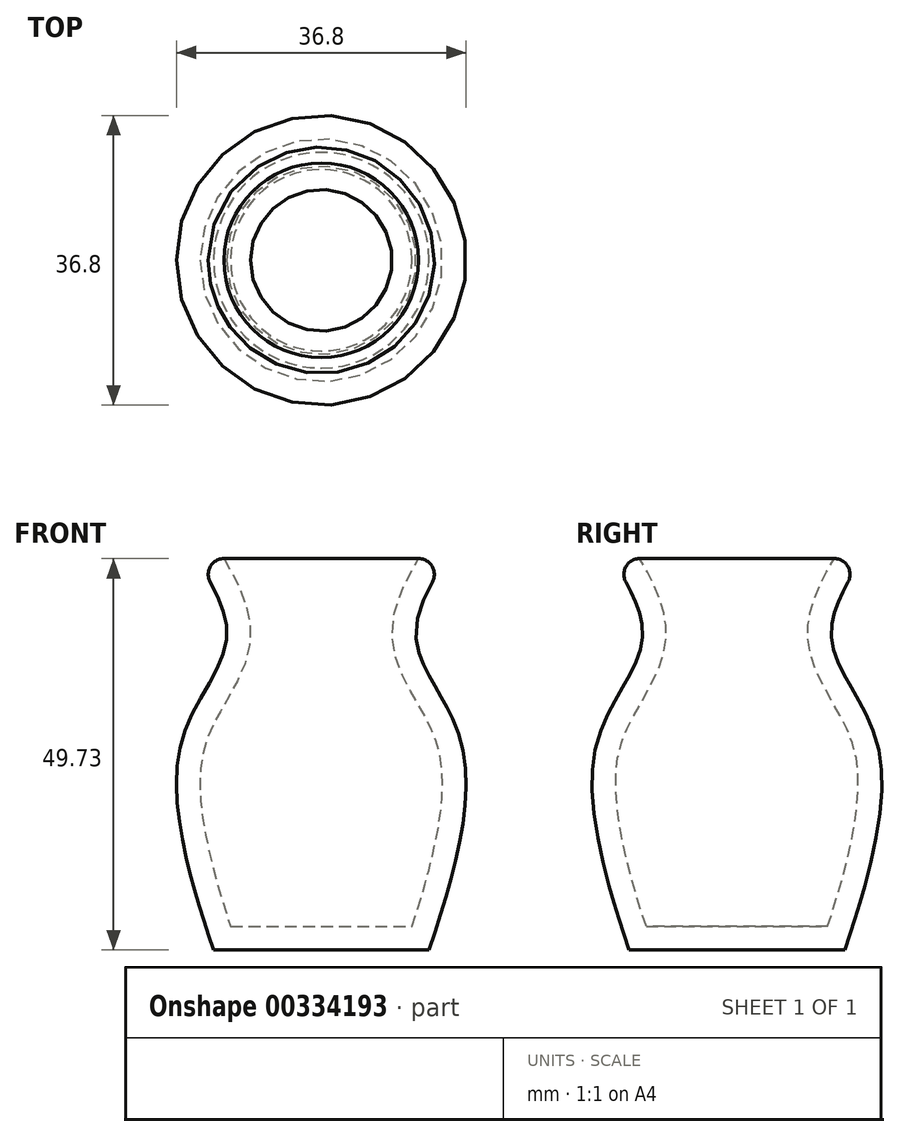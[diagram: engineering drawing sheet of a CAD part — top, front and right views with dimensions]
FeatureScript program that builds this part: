
annotation { "Feature Type Name" : "Feature", "Feature Type Description" : "" }
export const myFeature = defineFeature(function(context is Context, id is Id, definition is map)
    precondition{}
    {
        {
            var Q0;
            Q0=qCreatedBy(makeId("Front.planeOp"),FACE);
            var sketch = newSketch(context, id + "F0", { "sketchPlane" : qUnion([Q0])});
            skFitSpline(sketch, "E0", {"points": [v(15.88, 49.73) * mm, v(12.05, 39.33) * mm, v(17.52, 27.28) * mm, v(17.16, 11.77) * mm, v(13.69, 0) * mm], "startDerivative": vector(-27.69, -45.07) * mm, "endDerivative": vector(-15.22, -45.72) * mm});
            skLineSegment(sketch, "E1", {"start": v(0, 0) * mm, "end": v(0, 52.4) * mm, "construction": true});
            skLineSegment(sketch, "E2", {"start": v(15.88, 49.73) * mm, "end": v(0, 49.73) * mm});
            skLineSegment(sketch, "E3", {"start": v(13.69, 0) * mm, "end": v(0, 0) * mm});
            skLineSegment(sketch, "E4", {"start": v(0, 49.73) * mm, "end": v(0, 0) * mm});
            skSolve(sketch);
        }
        {
            var Q0;
            Q0 = qSketchRegion(id + "F0", true);
            var Q1;
            Q1=sQuery(id+"F0.wireOp",EDGE,"E1");
            revolve(context, id + "F1", {"entities" : qUnion([Q0]), "axis" : qUnion([Q1]), "revolveType" : RevolveType.FULL});
        }
        {
            var Q0;
            Q0=makeQuery(id+"F1.opRevolve","SWEPT_FACE",FACE,{"disambiguationData":[OSD([sQuery(id+"F0.wireOp",EDGE,"E2")])]});
            shell(context, id + "F2", {"entities" : qUnion([Q0]), "thickness" : 3 * mm});
        }
        {
            var Q0;
            Q0=makeQuery(id+"F1.opRevolve","SWEPT_EDGE",EDGE,{"disambiguationData":[OSD([sQuery(id+"F0.wireOp",EDGE,"E0"),sQuery(id+"F0.wireOp",EDGE,"E2")])]});
            fillet(context, id + "F3", {"entities" : qUnion([Q0]), "radius" : 2 * mm, "tangentPropagation" : true, "allowEdgeOverflow" : false});
        }
    });
